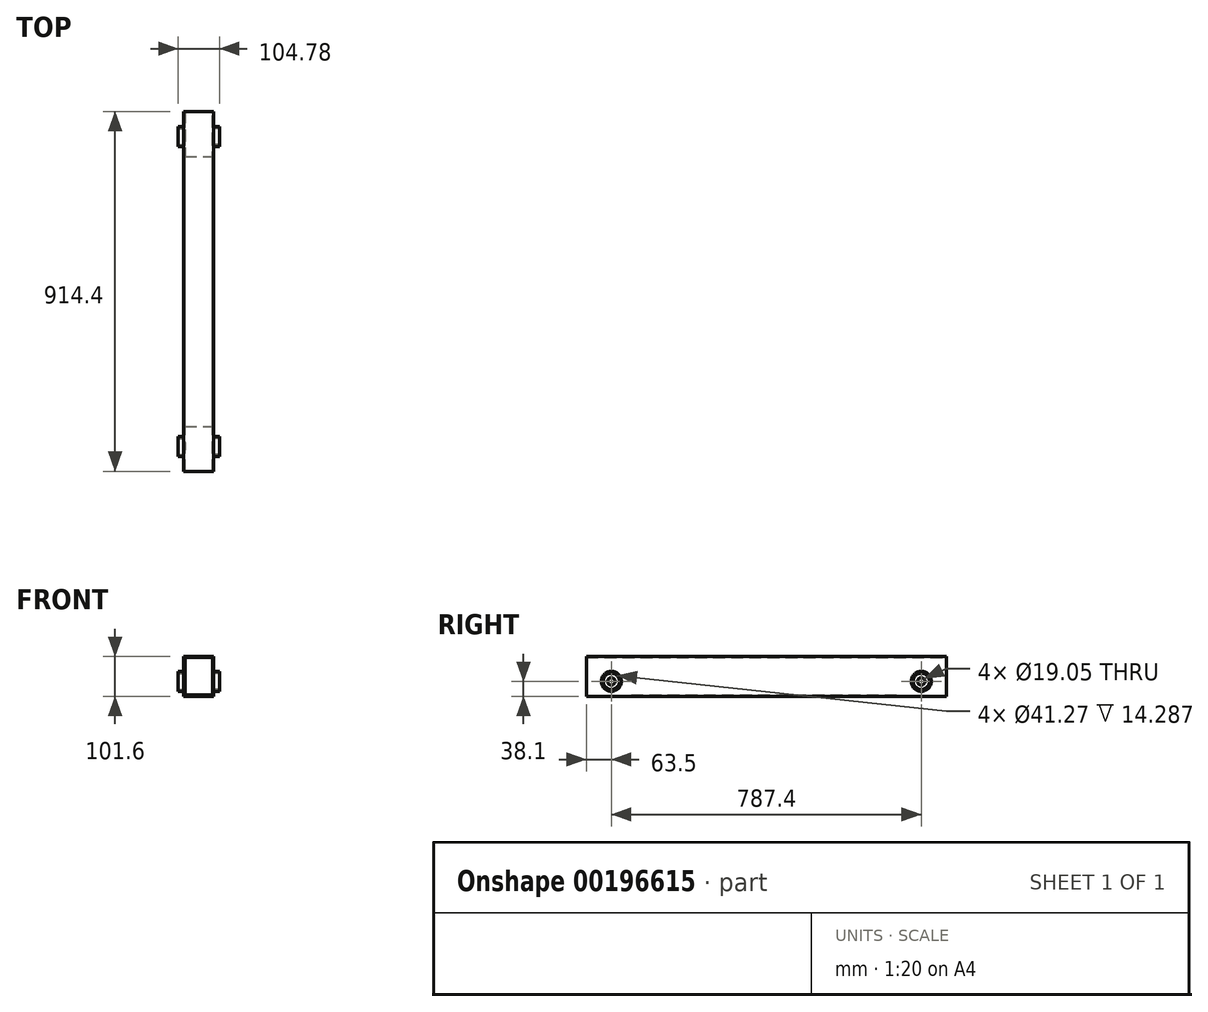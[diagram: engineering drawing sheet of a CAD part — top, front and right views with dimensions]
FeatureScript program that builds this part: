
annotation { "Feature Type Name" : "Feature", "Feature Type Description" : "" }
export const myFeature = defineFeature(function(context is Context, id is Id, definition is map)
    precondition{}
    {
        {
            var Q0;
            Q0=qCreatedBy(makeId("Front.planeOp"),FACE);
            var sketch = newSketch(context, id + "F0", { "sketchPlane" : qUnion([Q0])});
            skLineSegment(sketch, "E0.bottom", {"start": v(0, 0) * mm, "end": v(76.2, 0) * mm});
            skLineSegment(sketch, "E0.top", {"start": v(0, 101.6) * mm, "end": v(76.2, 101.6) * mm});
            skLineSegment(sketch, "E0.left", {"start": v(0, 0) * mm, "end": v(0, 101.6) * mm});
            skLineSegment(sketch, "E0.right", {"start": v(76.2, 0) * mm, "end": v(76.2, 101.6) * mm});
            skLineSegment(sketch, "E1.bottom", {"start": v(3.17, 98.43) * mm, "end": v(73.03, 98.43) * mm});
            skLineSegment(sketch, "E1.top", {"start": v(3.17, 3.18) * mm, "end": v(73.03, 3.18) * mm});
            skLineSegment(sketch, "E1.left", {"start": v(3.17, 98.43) * mm, "end": v(3.17, 3.17) * mm});
            skLineSegment(sketch, "E1.right", {"start": v(73.03, 98.43) * mm, "end": v(73.03, 3.17) * mm});
            skSolve(sketch);
        }
        {
            var Q0;
            Q0=makeQuery(id+"F0.imprint","IMPRINT",FACE,{"disambiguationData":[TD([[makeQuery(id+"F0.imprint","IMPRINT",EDGE,{"derivedFrom":sQuery(id+"F0.wireOp",EDGE,"E0.bottom")}),1.0]])]});
            extrude(context, id + "F1", {"entities" : qUnion([Q0]), "depth" : 914.4 * mm});
        }
        {
            var Q0;
            Q0=qCreatedBy(makeId("Right.planeOp"),FACE);
            var sketch = newSketch(context, id + "F2", { "sketchPlane" : qUnion([Q0])});
            skCircle(sketch, "E2", {"center": v(-850.9, 38.1) * mm, "radius": 9.53 * mm});
            skCircle(sketch, "E3", {"center": v(-63.5, 38.1) * mm, "radius": 9.53 * mm});
            skSolve(sketch);
        }
        {
            var Q0;
            Q0 = qSketchRegion(id + "F2", true);
            extrude(context, id + "F3", {"entities" : qUnion([Q0]), "operationType" : NewBodyOperationType.REMOVE, "depth" : 76.2 * mm});
        }
        {
            var Q0;
            Q0=qCreatedBy(makeId("Top.planeOp"),FACE);
            var sketch = newSketch(context, id + "F4", { "sketchPlane" : qUnion([Q0])});
            skLineSegment(sketch, "E4.bottom", {"start": v(3.18, -914.4) * mm, "end": v(73.03, -914.4) * mm});
            skLineSegment(sketch, "E4.top", {"start": v(3.17, -800.1) * mm, "end": v(73.03, -800.1) * mm});
            skLineSegment(sketch, "E4.left", {"start": v(3.18, -914.4) * mm, "end": v(3.17, -800.1) * mm});
            skLineSegment(sketch, "E4.right", {"start": v(73.03, -914.4) * mm, "end": v(73.03, -800.1) * mm});
            skLineSegment(sketch, "E5.bottom", {"start": v(3.17, 0) * mm, "end": v(73.03, 0) * mm});
            skLineSegment(sketch, "E5.top", {"start": v(3.18, -114.3) * mm, "end": v(73.03, -114.3) * mm});
            skLineSegment(sketch, "E5.left", {"start": v(3.17, 0) * mm, "end": v(3.18, -114.3) * mm});
            skLineSegment(sketch, "E5.right", {"start": v(73.03, 0) * mm, "end": v(73.03, -114.3) * mm});
            skSolve(sketch);
        }
        {
            var Q0;
            Q0 = qSketchRegion(id + "F4", true);
            extrude(context, id + "F5", {"entities" : qUnion([Q0]), "operationType" : NewBodyOperationType.REMOVE, "depth" : 3.17 * mm});
        }
        {
            var Q0;
            Q0=makeQuery(id+"F1.opExtrude","SWEPT_FACE",FACE,{"disambiguationData":[OSD([sQuery(id+"F0.wireOp",EDGE,"E0.right")])]});
            var sketch = newSketch(context, id + "F6", { "sketchPlane" : qUnion([Q0])});
            skCircle(sketch, "E6", {"center": v(-850.9, 38.1) * mm, "radius": 20.64 * mm});
            skCircle(sketch, "E7", {"center": v(-63.5, 38.1) * mm, "radius": 20.64 * mm});
            skCircle(sketch, "E8", {"center": v(-850.9, 38.1) * mm, "radius": 25.4 * mm});
            skCircle(sketch, "E9", {"center": v(-63.5, 38.1) * mm, "radius": 25.4 * mm});
            skSolve(sketch);
        }
        {
            var Q0;
            Q0=makeQuery(id+"F6.imprint","IMPRINT",FACE,{"disambiguationData":[TD([[makeQuery(id+"F6.imprint","IMPRINT",EDGE,{"derivedFrom":sQuery(id+"F6.wireOp",EDGE,"E6")}),-1.0]])]});
            var Q1;
            Q1=makeQuery(id+"F6.imprint","IMPRINT",FACE,{"disambiguationData":[TD([[makeQuery(id+"F6.imprint","IMPRINT",EDGE,{"derivedFrom":sQuery(id+"F6.wireOp",EDGE,"E7")}),-1.0]])]});
            extrude(context, id + "F7", {"entities" : qUnion([Q0, Q1]), "operationType" : NewBodyOperationType.ADD, "depth" : 14.29 * mm});
        }
        {
            var Q0;
            Q0=makeQuery(id+"F1.opExtrude","SWEPT_FACE",FACE,{"disambiguationData":[OSD([sQuery(id+"F0.wireOp",EDGE,"E0.left")])]});
            var sketch = newSketch(context, id + "F8", { "sketchPlane" : qUnion([Q0])});
            skCircle(sketch, "E10", {"center": v(63.5, 38.1) * mm, "radius": 20.64 * mm});
            skCircle(sketch, "E11", {"center": v(850.9, 38.1) * mm, "radius": 20.64 * mm});
            skCircle(sketch, "E12", {"center": v(850.9, 38.1) * mm, "radius": 25.4 * mm});
            skCircle(sketch, "E13", {"center": v(63.5, 38.1) * mm, "radius": 25.4 * mm});
            skSolve(sketch);
        }
        {
            var Q0;
            Q0=makeQuery(id+"F8.imprint","IMPRINT",FACE,{"disambiguationData":[TD([[makeQuery(id+"F8.imprint","IMPRINT",EDGE,{"derivedFrom":sQuery(id+"F8.wireOp",EDGE,"E10")}),-1.0]])]});
            var Q1;
            Q1=makeQuery(id+"F8.imprint","IMPRINT",FACE,{"disambiguationData":[TD([[makeQuery(id+"F8.imprint","IMPRINT",EDGE,{"derivedFrom":sQuery(id+"F8.wireOp",EDGE,"E11")}),-1.0]])]});
            extrude(context, id + "F9", {"entities" : qUnion([Q0, Q1]), "operationType" : NewBodyOperationType.ADD, "depth" : 14.29 * mm});
        }
    });
